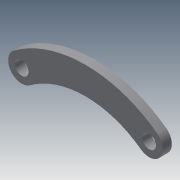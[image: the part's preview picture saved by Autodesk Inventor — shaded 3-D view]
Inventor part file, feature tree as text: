
AUTODESK INVENTOR PART (.ipt)
format: ipt  version: 2013 (Build 170138000, 138)  size: 89,088 bytes
history: native  units: mm
features: extrude x1, sketch x1
ambient origin geometry x8: Origin, YZ Plane, XZ Plane, XY Plane, X Axis, Y Axis, Z Axis, Center Point
bodies: Solid1 (feature_tree)
feature tree (2):
  extrude  "Extrusion1"  Depth=6.0mm
  sketch  "Sketch1"  dims[d1=6.0mm d2=6.0mm d3=3.0mm d4=3.0mm d5=19.0mm d7=6.0mm d8=2.0mm d9=0.0mm]
